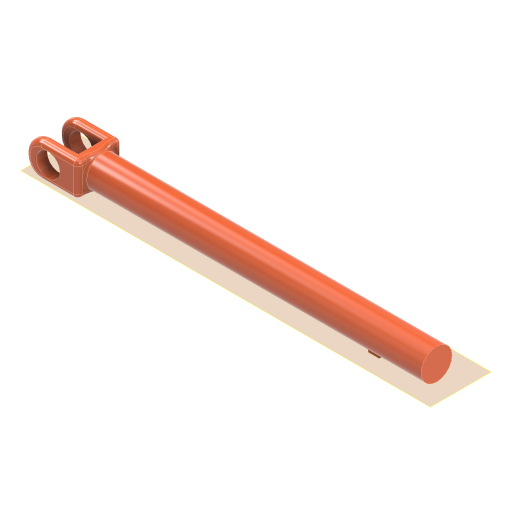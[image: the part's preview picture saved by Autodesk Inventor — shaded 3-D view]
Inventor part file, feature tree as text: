
AUTODESK INVENTOR PART (.ipt)
format: ipt  version: 2024 (Build 280153000, 153)  size: 254,464 bytes
history: native  units: mm
features: sketch x7, extrude x5, fillet x4, other x4
ambient origin geometry x8: Origin, YZ Plane, XZ Plane, XY Plane, X Axis, Y Axis, Z Axis, Center Point
bodies: Solido1 (feature_tree)
feature tree (20):
  sketch  "Schizzo1"
  extrude  "Estrusione1"  Depth=18.0mm
  extrude  "Estrusione4"  Depth=136.5mm
  extrude  "Estrusione5"  Depth=7.0mm
  sketch  "Schizzo9"
  extrude  "Estrusione6"  Depth=14.0mm
  fillet  "Raccordo1"  Radius=152.07mm
  fillet  "Raccordo2"  Radius=20.0mm
  other  "Raccordo faccia1"
  fillet  "Raccordo3"  Radius=10.0mm
  fillet  "Raccordo4"  Radius=15.0mm
  other  "Piano di lavoro3"
  other  "Piano di lavoro4"
  other  "Piano di lavoro5"
  extrude  "Estrusione10"  Depth=7.5mm
  sketch  "Schizzo2"
  sketch  "Schizzo7"
  sketch  "Schizzo8"
  sketch  "Schizzo10"
  sketch  "Schizzo15"
